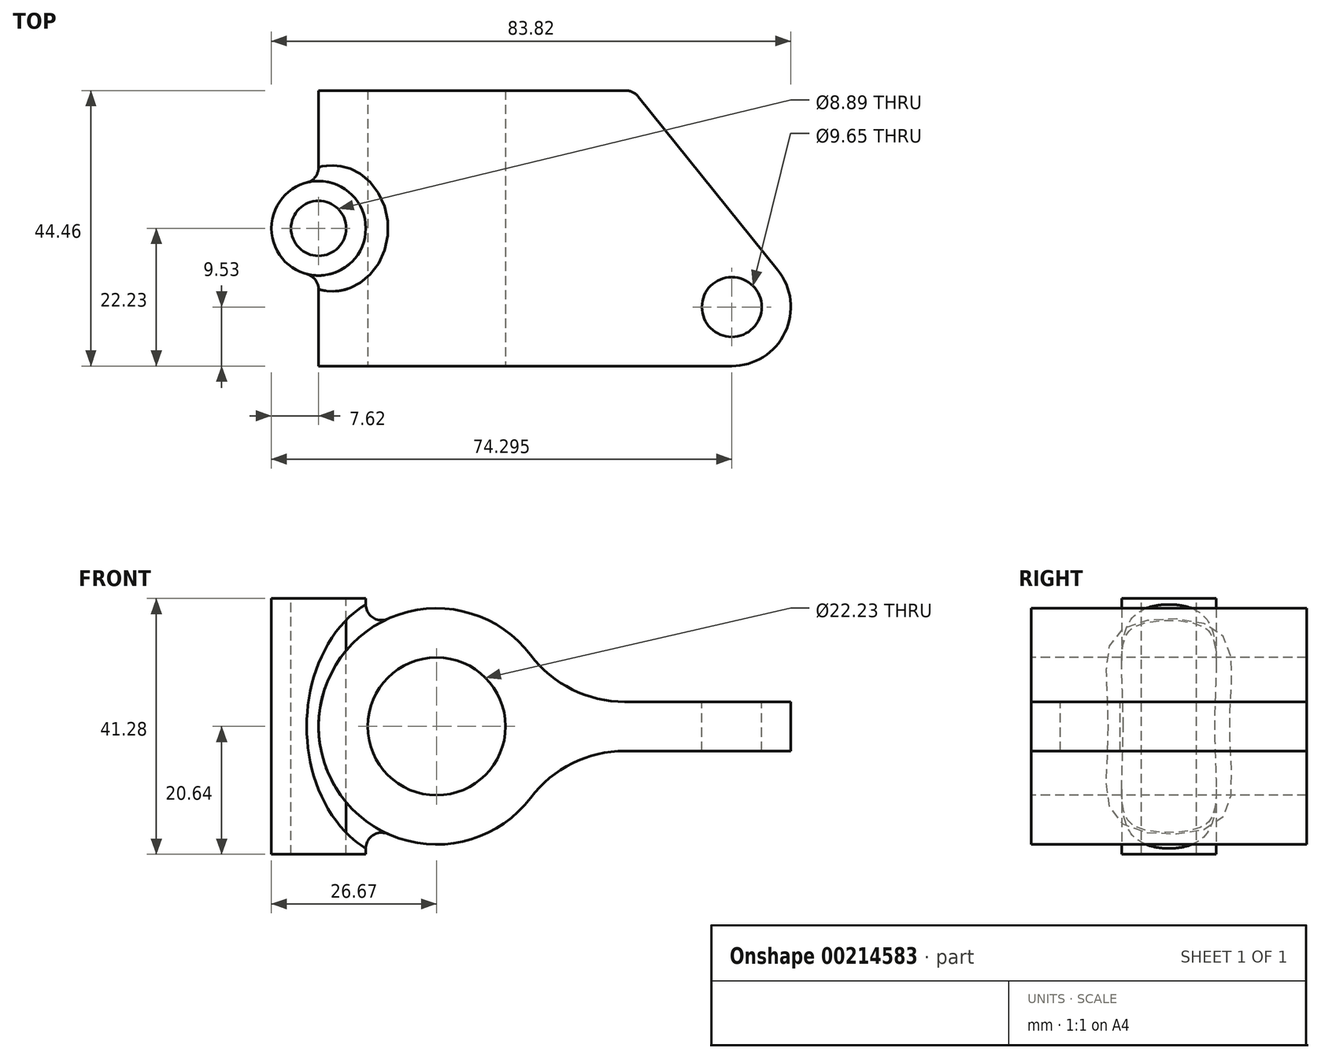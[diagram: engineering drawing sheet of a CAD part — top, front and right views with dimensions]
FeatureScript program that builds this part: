
annotation { "Feature Type Name" : "Feature", "Feature Type Description" : "" }
export const myFeature = defineFeature(function(context is Context, id is Id, definition is map)
    precondition{}
    {
        {
            var Q0;
            Q0=qCreatedBy(makeId("Front.planeOp"),FACE);
            var sketch = newSketch(context, id + "F0", { "sketchPlane" : qUnion([Q0])});
            skCircle(sketch, "E0", {"center": v(0, 0) * mm, "radius": 19.05 * mm});
            skSolve(sketch);
        }
        {
            var Q0;
            Q0=makeQuery(id+"F0.imprint","IMPRINT",FACE,{"disambiguationData":[TD([[makeQuery(id+"F0.imprint","IMPRINT",EDGE,{"derivedFrom":sQuery(id+"F0.wireOp",EDGE,"E0")}),1.0]])]});
            extrude(context, id + "F1", {"entities" : qUnion([Q0]), "depth" : 44.45 * mm, "symmetric" : true});
        }
        {
            var Q0;
            Q0=qCreatedBy(makeId("Top.planeOp"),FACE);
            var sketch = newSketch(context, id + "F2", { "sketchPlane" : qUnion([Q0])});
            skLineSegment(sketch, "E1.0", {"start": v(19.05, -22.23) * mm, "end": v(-19.05, -22.23) * mm});
            skLineSegment(sketch, "E1.1", {"start": v(19.05, 22.23) * mm, "end": v(-19.05, 22.23) * mm});
            skCircle(sketch, "E2", {"center": v(-19.05, 0) * mm, "radius": 7.62 * mm});
            skSolve(sketch);
        }
        {
            var Q0;
            Q0=makeQuery(id+"F2.imprint","IMPRINT",FACE,{"disambiguationData":[TD([[makeQuery(id+"F2.imprint","IMPRINT",EDGE,{"derivedFrom":sQuery(id+"F2.wireOp",EDGE,"E2")}),1.0]])]});
            extrude(context, id + "F3", {"entities" : qUnion([Q0]), "operationType" : NewBodyOperationType.ADD, "depth" : 41.27 * mm, "symmetric" : true});
        }
        {
            var Q0;
            Q0=qCreatedBy(makeId("Top.planeOp"),FACE);
            var sketch = newSketch(context, id + "F4", { "sketchPlane" : qUnion([Q0])});
            skLineSegment(sketch, "E3.0", {"start": v(19.05, 22.23) * mm, "end": v(-19.05, 22.23) * mm});
            skLineSegment(sketch, "E3.1", {"start": v(19.05, -22.23) * mm, "end": v(-19.05, -22.23) * mm});
            skLineSegment(sketch, "E4", {"start": v(0, -22.23) * mm, "end": v(0, 22.23) * mm});
            skLineSegment(sketch, "E5", {"start": v(0, 22.23) * mm, "end": v(31.75, 22.23) * mm});
            skLineSegment(sketch, "E6", {"start": v(31.75, 22.23) * mm, "end": v(55.05, -6.73) * mm});
            skLineSegment(sketch, "E7", {"start": v(19.05, -22.23) * mm, "end": v(47.63, -22.23) * mm});
            skArc(sketch, "E8", {"start": v(47.63, -22.23) * mm, "mid": v(56.22, -16.81) * mm, "end": v(55.05, -6.73) * mm});
            skSolve(sketch);
        }
        {
            var Q0;
            {var subQ3=sQuery(id+"F4.wireOp",EDGE,"E4");Q0=makeQuery(id+"F4.imprint","IMPRINT",FACE,{"disambiguationData":[TD([[makeQuery(id+"F4.imprint","IMPRINT",EDGE,{"derivedFrom":subQ3}),-1.0]])]});}
            extrude(context, id + "F5", {"entities" : qUnion([Q0]), "operationType" : NewBodyOperationType.ADD, "depth" : 7.94 * mm, "symmetric" : true});
        }
        {
            var Q0;
            Q0=makeQuery(id+"F3.opExtrude","CAP_FACE",FACE,{"disambiguationData":[OSD([sQuery(id+"F2.wireOp",EDGE,"E2")])],"isStart":false});
            var sketch = newSketch(context, id + "F6", { "sketchPlane" : qUnion([Q0])});
            skCircle(sketch, "E9.0", {"center": v(-19.05, 0) * mm, "radius": 4.44 * mm});
            skSolve(sketch);
        }
        {
            var Q0;
            Q0=makeQuery(id+"F6.imprint","IMPRINT",FACE,{"disambiguationData":[TD([[makeQuery(id+"F6.imprint","IMPRINT",EDGE,{"derivedFrom":sQuery(id+"F6.wireOp",EDGE,"E9.0")}),1.0]])]});
            extrude(context, id + "F7", {"entities" : qUnion([Q0]), "operationType" : NewBodyOperationType.REMOVE, "endBound" : BoundingType.THROUGH_ALL, "oppositeDirection" : true, "depth" : 25.4 * mm});
        }
        {
            var Q0;
            Q0=makeQuery(id+"F5.boolean.opBoolean","MERGE",FACE,{"derivedFrom":[makeQuery(id+"F1.opExtrude","CAP_FACE",FACE,{"disambiguationData":[OSD([sQuery(id+"F0.wireOp",EDGE,"E0")])],"isStart":false}),makeQuery(id+"F5.opExtrude","SWEPT_FACE",FACE,{"disambiguationData":[OSD([sQuery(id+"F4.wireOp",EDGE,"E3.1")])]})]});
            var sketch = newSketch(context, id + "F8", { "sketchPlane" : qUnion([Q0])});
            skCircle(sketch, "E10", {"center": v(0, 0) * mm, "radius": 11.11 * mm});
            skSolve(sketch);
        }
        {
            var Q0;
            Q0=makeQuery(id+"F8.imprint","IMPRINT",FACE,{"disambiguationData":[TD([[makeQuery(id+"F8.imprint","IMPRINT",EDGE,{"derivedFrom":sQuery(id+"F8.wireOp",EDGE,"E10")}),1.0]])]});
            extrude(context, id + "F9", {"entities" : qUnion([Q0]), "operationType" : NewBodyOperationType.REMOVE, "endBound" : BoundingType.THROUGH_ALL, "oppositeDirection" : true, "depth" : 25.4 * mm});
        }
        {
            var Q0;
            Q0=makeQuery(id+"F5.opExtrude","CAP_FACE",FACE,{"disambiguationData":[OSD([sQuery(id+"F4.wireOp",EDGE,"E3.1"),sQuery(id+"F4.wireOp",EDGE,"E4"),sQuery(id+"F4.wireOp",EDGE,"E5"),sQuery(id+"F4.wireOp",EDGE,"E6"),sQuery(id+"F4.wireOp",EDGE,"E8")])],"isStart":false});
            var sketch = newSketch(context, id + "F10", { "sketchPlane" : qUnion([Q0])});
            skCircle(sketch, "E11", {"center": v(47.63, -12.7) * mm, "radius": 4.83 * mm});
            skSolve(sketch);
        }
        {
            var Q0;
            Q0=makeQuery(id+"F10.imprint","IMPRINT",FACE,{"disambiguationData":[TD([[makeQuery(id+"F10.imprint","IMPRINT",EDGE,{"derivedFrom":sQuery(id+"F10.wireOp",EDGE,"E11")}),1.0]])]});
            extrude(context, id + "F11", {"entities" : qUnion([Q0]), "operationType" : NewBodyOperationType.ADD, "depth" : 25.4 * mm});
        }
        {
            var Q0;
            Q0=makeQuery(id+"F11.opExtrude","CAP_FACE",FACE,{"disambiguationData":[OSD([sQuery(id+"F10.wireOp",EDGE,"E11")])],"isStart":false});
            extrude(context, id + "F12", {"entities" : qUnion([Q0]), "operationType" : NewBodyOperationType.REMOVE, "endBound" : BoundingType.THROUGH_ALL, "oppositeDirection" : true, "depth" : 25.4 * mm});
        }
        {
            var Q0;
            Q0=makeQuery(id+"F5.boolean.opBoolean","INTERSECT",EDGE,{"derivedFrom":[makeQuery(id+"F1.opExtrude","SWEPT_FACE",FACE,{"disambiguationData":[OSD([sQuery(id+"F0.wireOp",EDGE,"E0")])]}),makeQuery(id+"F5.opExtrude","CAP_FACE",FACE,{"disambiguationData":[OSD([sQuery(id+"F4.wireOp",EDGE,"E3.1"),sQuery(id+"F4.wireOp",EDGE,"E4"),sQuery(id+"F4.wireOp",EDGE,"E5"),sQuery(id+"F4.wireOp",EDGE,"E6"),sQuery(id+"F4.wireOp",EDGE,"E8")])],"isStart":false})]});
            var Q1;
            Q1=makeQuery(id+"F5.boolean.opBoolean","INTERSECT",EDGE,{"derivedFrom":[makeQuery(id+"F1.opExtrude","SWEPT_FACE",FACE,{"disambiguationData":[OSD([sQuery(id+"F0.wireOp",EDGE,"E0")])]}),makeQuery(id+"F5.opExtrude","CAP_FACE",FACE,{"disambiguationData":[OSD([sQuery(id+"F4.wireOp",EDGE,"E3.1"),sQuery(id+"F4.wireOp",EDGE,"E4"),sQuery(id+"F4.wireOp",EDGE,"E5"),sQuery(id+"F4.wireOp",EDGE,"E6"),sQuery(id+"F4.wireOp",EDGE,"E8")])],"isStart":true})]});
            fillet(context, id + "F13", {"entities" : qUnion([Q0, Q1]), "radius" : 19.05 * mm, "tangentPropagation" : true, "allowEdgeOverflow" : false});
        }
        {
            var Q0;
            Q0=makeQuery(id+"F5.opExtrude","SWEPT_EDGE",EDGE,{"disambiguationData":[OSD([sQuery(id+"F4.wireOp",EDGE,"E5"),sQuery(id+"F4.wireOp",EDGE,"E6")])]});
            var Q1;
            Q1=makeQuery(id+"F3.boolean.opBoolean","INTERSECT",EDGE,{"derivedFrom":[makeQuery(id+"F1.opExtrude","SWEPT_FACE",FACE,{"disambiguationData":[OSD([sQuery(id+"F0.wireOp",EDGE,"E0")])]}),makeQuery(id+"F3.opExtrude","SWEPT_FACE",FACE,{"disambiguationData":[OSD([sQuery(id+"F2.wireOp",EDGE,"E2")])]})]});
            fillet(context, id + "F14", {"entities" : qUnion([Q0, Q1]), "radius" : 2.54 * mm, "tangentPropagation" : true, "allowEdgeOverflow" : false});
        }
    });
